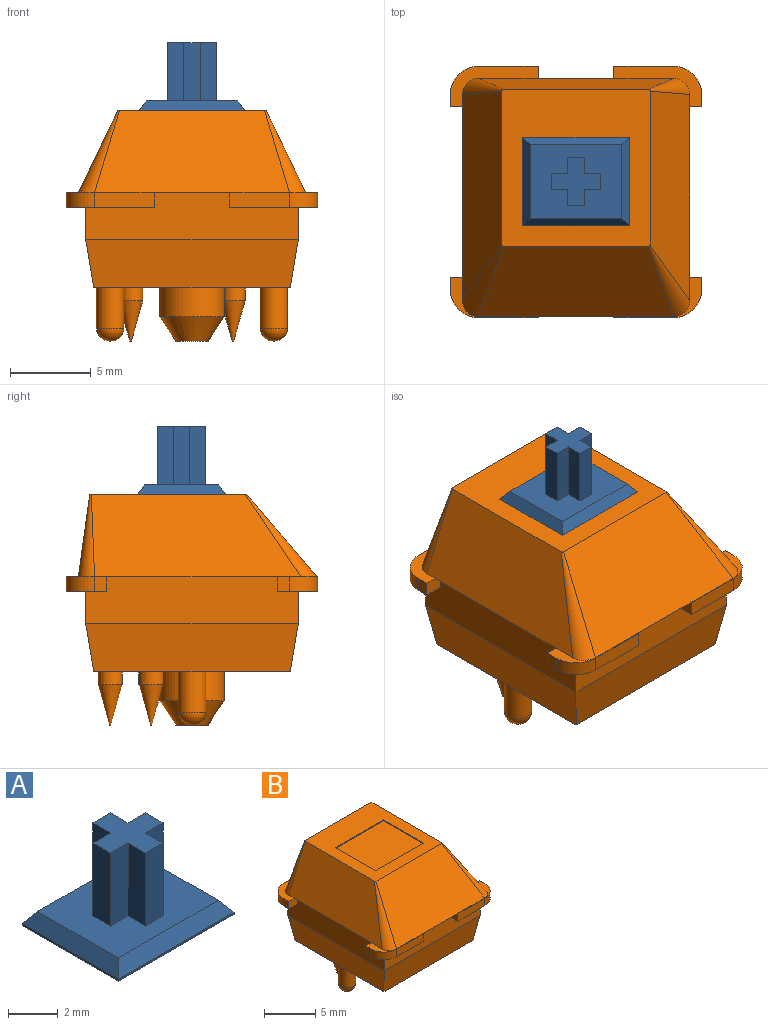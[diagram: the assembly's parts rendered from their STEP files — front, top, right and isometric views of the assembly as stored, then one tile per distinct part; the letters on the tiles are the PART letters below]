
ASSEMBLY  parts=2 mates=1
PART A: 23 faces, bbox 6.6x5.5x4.3 mm
  f0: plane 3x3mm, normal (0,0,1), area 5mm2, adj f1,f2,f3,f4,f5,f6,f7,f8
  f1: plane 3.6x1mm, normal (0,1,0), area 3.6mm2, adj f0,f2,f12,f13
  f2: plane 3.6x1mm, normal (-1,0,0), area 3.6mm2, adj f0,f1,f3,f13
  f3: plane 3.6x1mm, normal (0,-1,0), area 3.6mm2, adj f0,f2,f4,f13
  f4: plane 3.6x1mm, normal (-1,0,0), area 3.6mm2, adj f0,f3,f5,f13
  f5: plane 3.6x1mm, normal (0,-1,0), area 3.6mm2, adj f0,f4,f6,f13
  f6: plane 3.6x1mm, normal (1,0,0), area 3.6mm2, adj f0,f5,f7,f13
  f7: plane 3.6x1mm, normal (0,-1,0), area 3.6mm2, adj f0,f6,f8,f13
  f8: plane 3.6x1mm, normal (1,0,0), area 3.6mm2, adj f0,f7,f9,f13
  f9: plane 3.6x1mm, normal (0,1,0), area 3.6mm2, adj f0,f8,f10,f13
  f10: plane 3.6x1mm, normal (1,0,0), area 3.6mm2, adj f0,f9,f11,f13
  f11: plane 3.6x1mm, normal (0,1,0), area 3.6mm2, adj f0,f10,f12,f13
  f12: plane 3.6x1mm, normal (-1,0,0), area 3.6mm2, adj f0,f1,f11,f13
  f13: plane 5.7x4.6mm, normal (0,0,1), area 21.2mm2, adj f1,f2,f3,f4,f5,f6,f7,f8
  f14: plane 6.6x0.6mm, normal (0,0.8,0.6), area 4.6mm2, adj f13,f15,f17,f19
  f15: plane 5.5x0.6mm, normal (0.8,0,0.6), area 3.8mm2, adj f13,f14,f16,f20
  f16: plane 6.6x0.6mm, normal (0,-0.8,0.6), area 4.6mm2, adj f13,f15,f17,f21
  f17: plane 5.5x0.6mm, normal (-0.8,0,0.6), area 3.8mm2, adj f13,f14,f16,f18
  f18: plane 5.5x0.1mm, normal (-1,0,0), area 0.5mm2, adj f17,f19,f21,f22
  f19: plane 6.6x0.1mm, normal (0,1,0), area 0.7mm2, adj f14,f18,f20,f22
  f20: plane 5.5x0.1mm, normal (1,0,0), area 0.5mm2, adj f15,f19,f21,f22
  f21: plane 6.6x0.1mm, normal (0,-1,0), area 0.7mm2, adj f16,f18,f20,f22
  f22: plane 6.6x5.5mm, normal (0,0,-1), area 36.3mm2, adj f18,f19,f20,f21
PART B: 70 faces, bbox 15.7x15.7x14.4 mm
  f0: plane 9.76x9.21mm, normal (0,0,1), area 53.4mm2, adj f57,f58,f59,f60,f61,f62,f63,f64
  f1: plane 5.53x2.58mm, normal (0,0,1), area 1.7mm2, adj f41,f42,f43,f44,f45,f62,f63,f64
  f2: plane 5.53x2.58mm, normal (0,0,1), area 1.7mm2, adj f47,f48,f49,f50,f51,f57,f58,f64
  f3: plane 5.53x2.58mm, normal (0,0,1), area 5mm2, adj f29,f30,f31,f32,f33,f58,f59,f60
  f4: plane 5.53x2.58mm, normal (0,0,1), area 5mm2, adj f35,f36,f37,f38,f39,f60,f61,f62
  f5: plane 13.2x2.9mm, normal (-1,0,0), area 35.9mm2, adj f6,f8,f11,f33,f34,f48,f52,f54
  f6: plane 13.2x2.9mm, normal (0,-1,0), area 30.6mm2, adj f5,f7,f12,f42,f46,f47,f52,f55
  f7: plane 13.2x2.9mm, normal (1,0,0), area 35.9mm2, adj f6,f8,f13,f35,f40,f41,f46,f56
  f8: plane 13.2x2.9mm, normal (0,1,0), area 30.6mm2, adj f5,f7,f10,f29,f34,f39,f40,f53
  f9: plane 12.2x12.2mm, normal (0,0,-1), area 128.2mm2, adj f10,f11,f12,f13,f14,f16,f18,f20
  f10: plane 13.2x3mm, normal (0,0.99,-0.16), area 38.6mm2, adj f8,f9,f11,f13
  f11: plane 13.2x3mm, normal (-0.99,0,-0.16), area 38.6mm2, adj f5,f9,f10,f12
  f12: plane 13.2x3mm, normal (0,-0.99,-0.16), area 38.6mm2, adj f6,f9,f11,f13
  f13: plane 13.2x3mm, normal (0.99,0,-0.16), area 38.6mm2, adj f7,f9,f10,f12
  f14: cylinder r=2mm len=4mm, axis (0,0,1), area 22.6mm2, adj f9,f24
  f15: plane 2x2mm, normal (0,0,-1), area 3.1mm2, adj f24
  f16: cylinder r=0.85mm len=2.5mm, axis (0,0,1), area 13.4mm2, adj f9,f25
  f17: plane 0.1x0.1mm, normal (0,0,-1), area 0mm2, adj f25
  f18: cylinder r=0.75mm len=1.5mm, axis (0,0,1), area 3.8mm2, adj f9,f27
  f19: plane 0.1x0.1mm, normal (0,0,-1), area 0mm2, adj f27
  f20: cylinder r=0.75mm len=1.5mm, axis (0,0,1), area 3.8mm2, adj f9,f28
  f21: plane 0.1x0.1mm, normal (0,0,-1), area 0mm2, adj f28
  f22: cylinder r=0.85mm len=2.5mm, axis (0,0,1), area 13.4mm2, adj f9,f26
  f23: plane 0.1x0.1mm, normal (0,0,-1), area 0mm2, adj f26
  f24: cone r=2mm half-angle=33.7deg, axis (0,0,1), area 17mm2, adj f14,f15
  f25: torus R=0.05mm, axis (0,0,1), area 4.4mm2, adj f16,f17
  f26: torus R=0.05mm, axis (0,0,1), area 4.4mm2, adj f22,f23
  f27: cone r=0.75mm half-angle=15.6deg, axis (0,0,1), area 6.5mm2, adj f18,f19
  f28: cone r=0.75mm half-angle=15.6deg, axis (0,0,1), area 6.5mm2, adj f20,f21
  f29: plane 1.2x0.9mm, normal (1,0,0), area 1.1mm2, adj f3,f8,f30,f34,f53
  f30: plane 3.7x0.9mm, normal (0,1,0), area 3.3mm2, adj f3,f29,f31,f34
  f31: cylinder r=1.75mm len=1.75mm, axis (0,0,-1), area 2.5mm2, adj f3,f30,f32,f34
  f32: plane 0.9x0.75mm, normal (-1,0,0), area 0.7mm2, adj f3,f31,f33,f34
  f33: plane 1.2x0.9mm, normal (0,-1,0), area 1.1mm2, adj f3,f5,f32,f34,f54
  f34: plane 5.45x2.5mm, normal (0,0,-1), area 7.4mm2, adj f5,f8,f29,f30,f31,f32,f33
  f35: plane 1.2x0.9mm, normal (0,-1,0), area 1.1mm2, adj f4,f7,f36,f40,f56
  f36: plane 0.9x0.75mm, normal (1,0,0), area 0.7mm2, adj f4,f35,f37,f40
  f37: cylinder r=1.75mm len=1.75mm, axis (0,0,-1), area 2.5mm2, adj f4,f36,f38,f40
  f38: plane 3.7x0.9mm, normal (0,1,0), area 3.3mm2, adj f4,f37,f39,f40
  f39: plane 1.2x0.9mm, normal (-1,0,0), area 1.1mm2, adj f4,f8,f38,f40,f53
  f40: plane 5.45x2.5mm, normal (0,0,-1), area 7.4mm2, adj f7,f8,f35,f36,f37,f38,f39
  f41: plane 1.2x0.9mm, normal (0,1,0), area 1.1mm2, adj f1,f7,f45,f46,f56
  f42: plane 1.2x0.9mm, normal (-1,0,0), area 1.1mm2, adj f1,f6,f43,f46,f55
  f43: plane 3.7x0.9mm, normal (0,-1,0), area 3.3mm2, adj f1,f42,f44,f46
  f44: cylinder r=1.75mm len=1.75mm, axis (0,0,-1), area 2.5mm2, adj f1,f43,f45,f46
  f45: plane 0.9x0.75mm, normal (1,0,0), area 0.7mm2, adj f1,f41,f44,f46
  f46: plane 5.45x2.5mm, normal (0,0,-1), area 7.4mm2, adj f6,f7,f41,f42,f43,f44,f45
  f47: plane 1.2x0.9mm, normal (1,0,0), area 1.1mm2, adj f2,f6,f51,f52,f55
  f48: plane 1.2x0.9mm, normal (0,1,0), area 1.1mm2, adj f2,f5,f49,f52,f54
  f49: plane 0.9x0.75mm, normal (-1,0,0), area 0.7mm2, adj f2,f48,f50,f52
  f50: cylinder r=1.75mm len=1.75mm, axis (0,0,-1), area 2.5mm2, adj f2,f49,f51,f52
  f51: plane 3.7x0.9mm, normal (0,-1,0), area 3.3mm2, adj f2,f47,f50,f52
  f52: plane 5.45x2.5mm, normal (0,0,-1), area 7.4mm2, adj f5,f6,f47,f48,f49,f50,f51
  f53: plane 4.7x0.45mm, normal (0,0,-1), area 2.1mm2, adj f8,f29,f39,f60
  f54: plane 10.6x0.45mm, normal (0,0,-1), area 4.8mm2, adj f5,f33,f48,f58
  f55: plane 4.7x1.15mm, normal (0,0,-1), area 5.4mm2, adj f6,f42,f47,f64
  f56: plane 10.6x0.45mm, normal (0,0,-1), area 4.8mm2, adj f7,f35,f41,f62
  f57: bspline ~5.1x4.45mm, area 5.7mm2, adj f0,f2,f58,f64
  f58: plane 13x5.1mm, normal (-0.9,0,0.43), area 63.2mm2, adj f0,f2,f3,f54,f57,f59
  f59: bspline ~13.9x13.2mm, area 4.7mm2, adj f0,f3,f58,f60
  f60: plane 12.1x5.1mm, normal (0,0.99,0.14), area 54.3mm2, adj f0,f3,f4,f53,f59,f61
  f61: bspline ~13.9x13.2mm, area 4.7mm2, adj f0,f4,f60,f62
  f62: plane 13x5.1mm, normal (0.9,0,0.43), area 63.2mm2, adj f0,f1,f4,f56,f61,f63
  f63: bspline ~14.02x13.2mm, area 5.7mm2, adj f0,f1,f62,f64
  f64: plane 12.1x5.1mm, normal (0,-0.76,0.65), area 70.7mm2, adj f0,f1,f2,f55,f57,f63
  f65: plane 5.5x0.1mm, normal (1,0,0), area 0.5mm2, adj f0,f66,f68,f69
  f66: plane 6.6x0.1mm, normal (0,-1,0), area 0.7mm2, adj f0,f65,f67,f69
  f67: plane 5.5x0.1mm, normal (-1,0,0), area 0.5mm2, adj f0,f66,f68,f69
  f68: plane 6.6x0.1mm, normal (0,1,0), area 0.7mm2, adj f0,f65,f67,f69
  f69: plane 6.6x5.5mm, normal (0,0,1), area 36.3mm2, adj f65,f66,f67,f68
PLACE A t=(0.12,0.06,-5.97)mm
PLACE B t=(0.12,0.06,-5.97)mm
MATE fastened A.f22 <-> B.f69  axis (0,0,1) through (0.12,0.71,4.93)mm
